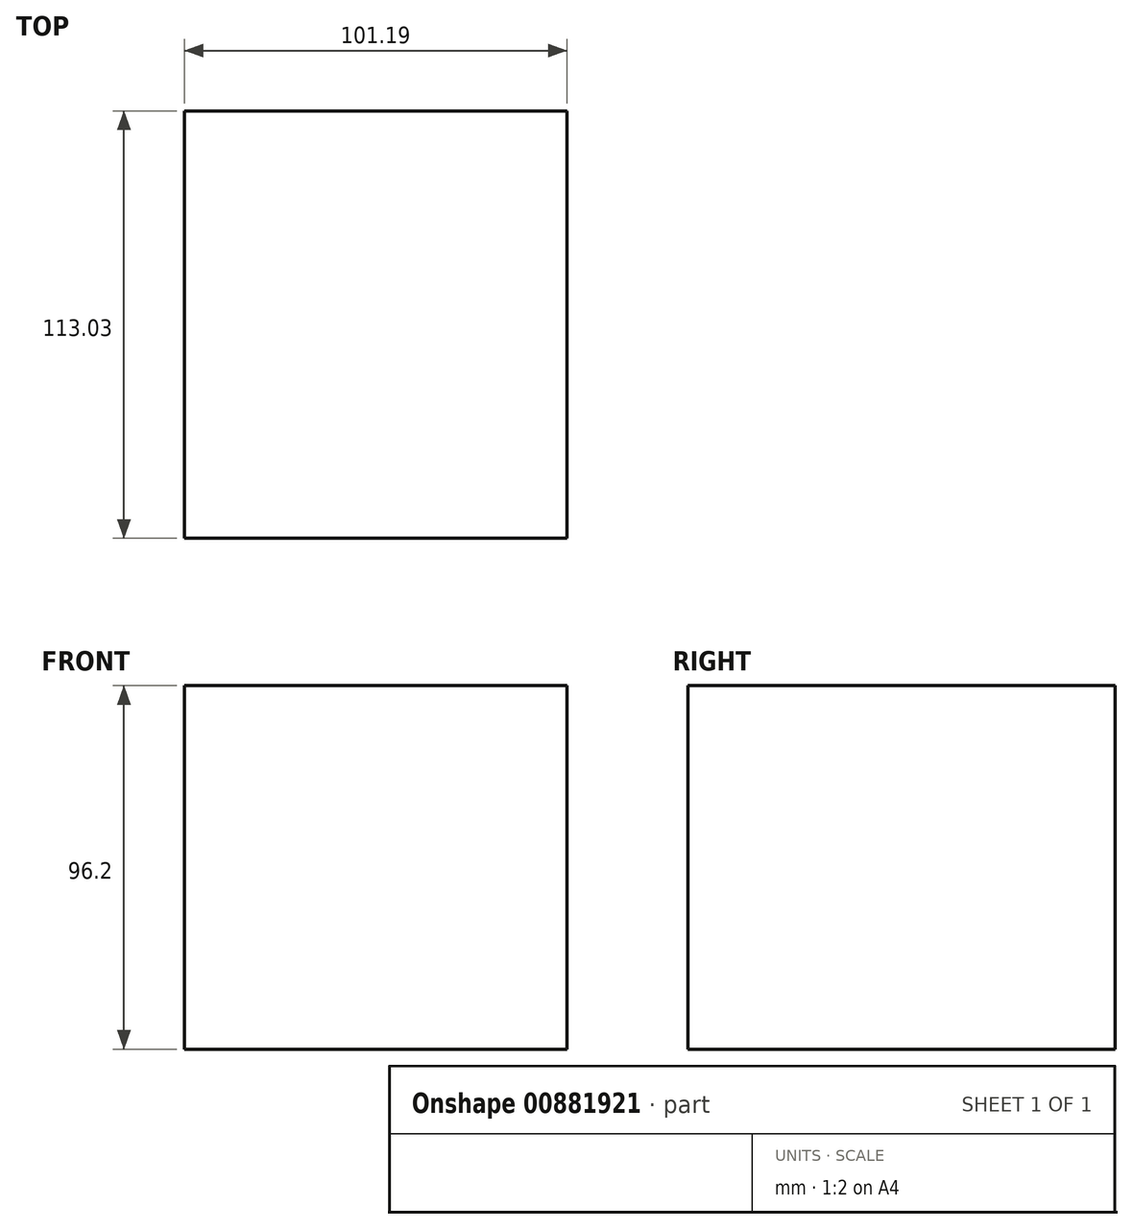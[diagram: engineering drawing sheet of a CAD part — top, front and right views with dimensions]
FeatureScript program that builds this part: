
annotation { "Feature Type Name" : "Feature", "Feature Type Description" : "" }
export const myFeature = defineFeature(function(context is Context, id is Id, definition is map)
    precondition{}
    {
        {
            var Q0;
            Q0=qCreatedBy(makeId("Front.planeOp"),FACE);
            var sketch = newSketch(context, id + "F0", { "sketchPlane" : qUnion([Q0])});
            skLineSegment(sketch, "E0.bottom", {"start": v(-47.53, 47.6) * mm, "end": v(53.66, 47.6) * mm});
            skLineSegment(sketch, "E0.top", {"start": v(-47.53, -48.6) * mm, "end": v(53.66, -48.6) * mm});
            skLineSegment(sketch, "E0.left", {"start": v(-47.53, 47.6) * mm, "end": v(-47.53, -48.6) * mm});
            skLineSegment(sketch, "E0.right", {"start": v(53.66, 47.6) * mm, "end": v(53.66, -48.6) * mm});
            skSolve(sketch);
        }
        {
            var Q0;
            Q0 = qSketchRegion(id + "F0", true);
            extrude(context, id + "F1", {"entities" : qUnion([Q0]), "oppositeDirection" : true, "depth" : 113.03 * mm, "offsetDistance" : 25.4 * mm});
        }
    });
